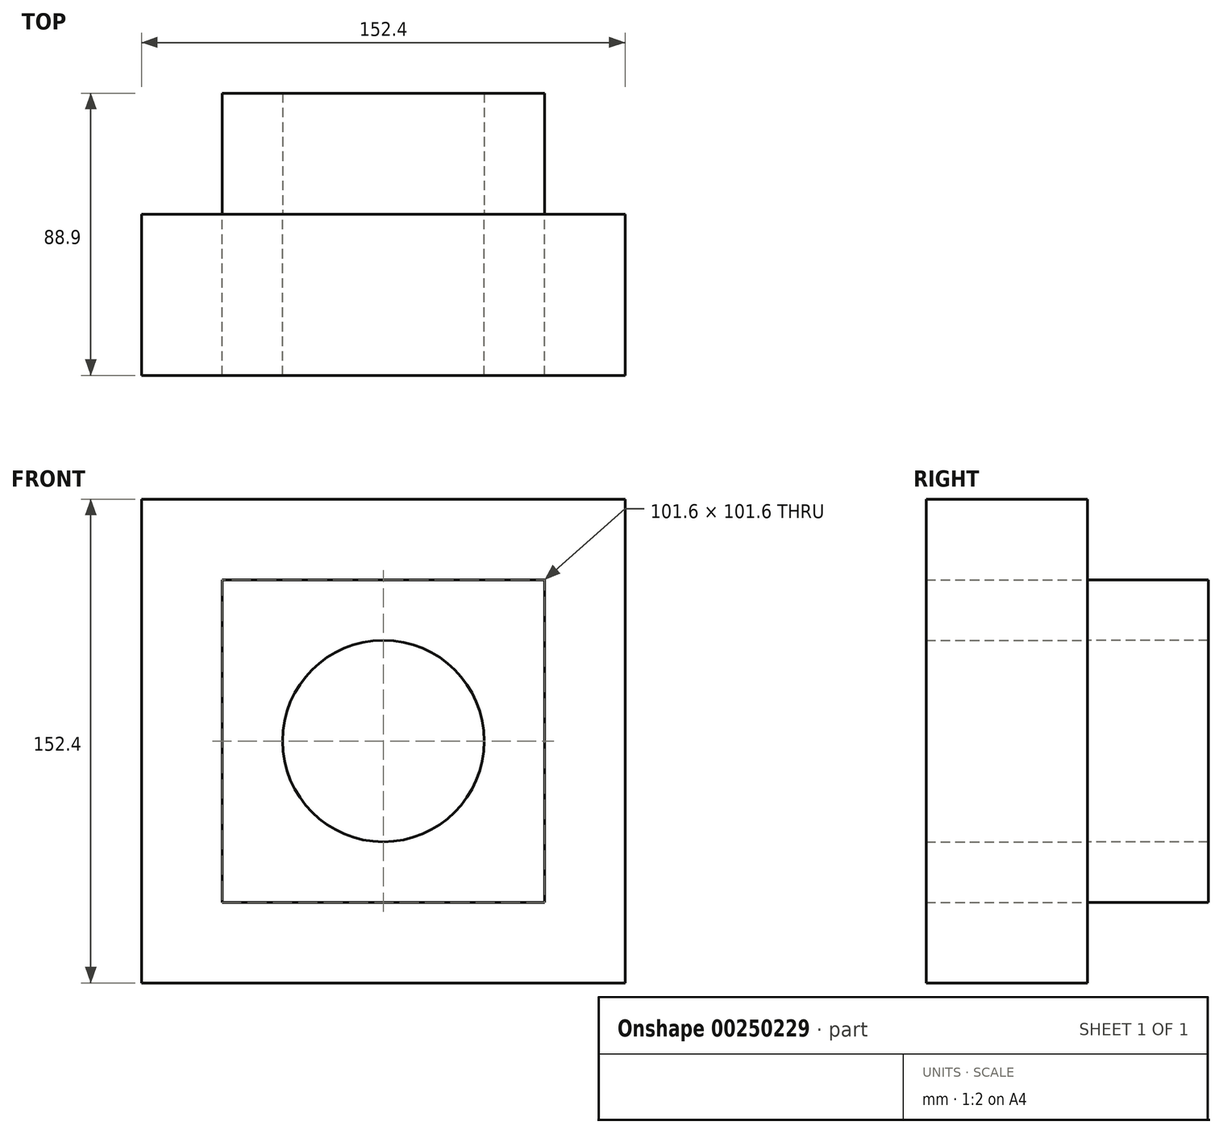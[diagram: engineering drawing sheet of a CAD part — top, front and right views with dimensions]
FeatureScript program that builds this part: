
annotation { "Feature Type Name" : "Feature", "Feature Type Description" : "" }
export const myFeature = defineFeature(function(context is Context, id is Id, definition is map)
    precondition{}
    {
        {
            var Q0;
            Q0=qCreatedBy(makeId("Front.planeOp"),FACE);
            var sketch = newSketch(context, id + "F0", { "sketchPlane" : qUnion([Q0])});
            skCircle(sketch, "E0", {"center": v(0, 0) * mm, "radius": 31.75 * mm});
            skLineSegment(sketch, "E1.bottom", {"start": v(50.8, 50.8) * mm, "end": v(-50.8, 50.8) * mm});
            skLineSegment(sketch, "E1.top", {"start": v(50.8, -50.8) * mm, "end": v(-50.8, -50.8) * mm});
            skLineSegment(sketch, "E1.left", {"start": v(50.8, 50.8) * mm, "end": v(50.8, -50.8) * mm});
            skLineSegment(sketch, "E1.right", {"start": v(-50.8, 50.8) * mm, "end": v(-50.8, -50.8) * mm});
            skLineSegment(sketch, "E2.bottom", {"start": v(76.2, 76.2) * mm, "end": v(-76.2, 76.2) * mm});
            skLineSegment(sketch, "E2.top", {"start": v(76.2, -76.2) * mm, "end": v(-76.2, -76.2) * mm});
            skLineSegment(sketch, "E2.left", {"start": v(76.2, 76.2) * mm, "end": v(76.2, -76.2) * mm});
            skLineSegment(sketch, "E2.right", {"start": v(-76.2, 76.2) * mm, "end": v(-76.2, -76.2) * mm});
            skSolve(sketch);
        }
        {
            var Q0;
            Q0=makeQuery(id+"F0.imprint","IMPRINT",FACE,{"disambiguationData":[TD([[makeQuery(id+"F0.imprint","IMPRINT",EDGE,{"derivedFrom":sQuery(id+"F0.wireOp",EDGE,"E0")}),-1.0]])]});
            extrude(context, id + "F1", {"entities" : qUnion([Q0]), "oppositeDirection" : true, "depth" : 38.1 * mm});
        }
        {
            var Q0;
            Q0=makeQuery(id+"F0.imprint","IMPRINT",FACE,{"disambiguationData":[TD([[makeQuery(id+"F0.imprint","IMPRINT",EDGE,{"derivedFrom":sQuery(id+"F0.wireOp",EDGE,"E1.bottom")}),-1.0]])]});
            var Q1;
            Q1=makeQuery(id+"F0.imprint","IMPRINT",FACE,{"disambiguationData":[TD([[makeQuery(id+"F0.imprint","IMPRINT",EDGE,{"derivedFrom":sQuery(id+"F0.wireOp",EDGE,"E0")}),1.0]])]});
            extrude(context, id + "F2", {"entities" : qUnion([Q0, Q1]), "depth" : 50.8 * mm});
        }
    });
